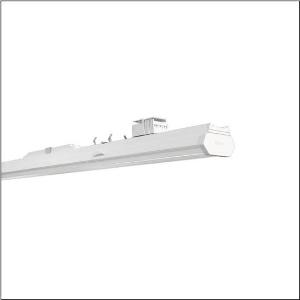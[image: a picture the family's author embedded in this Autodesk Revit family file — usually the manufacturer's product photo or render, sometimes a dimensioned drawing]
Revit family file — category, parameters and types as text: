
# Revit family: licross_11_protected_ho_51td12mn4f5m
name_source: partatom
category: Lighting Fixtures
units: mm (PartAtom-declared; Revit-internal decimal feet)

## family parameters
Cut with Voids When Loaded = No
Host = Face
Light Source = No
Part Type = Normal
Room Calculation Point = No
Round Connector Dimension = Use Diameter
Shared = No

## types (1)
- --- (1 x LED, 15820 lm, 87.4 W, 4000K)
    Apparent Load = 87 VA
    CIE Flux Codes = 70 91 97 98 100
    Color Rendering = 80
    Color Temperature = 4000K
    Default Elevation = 1800 mm
    Description = Licross 11 Protected HO, luminaire insert, of sheet steel, galvanised, coil coated, white, length: 1.500mm, width: 90mm, height: 101mm, LED rated luminous flux: 15.820lm, light colour: 840, SDCM (Standard Deviation of Colour Matching)MacAdam ≤ 2 SDCM (initial), control gear: ON/OFF Multilumen, with plug, 3-pole, with phase selection, mains connection: 220..240V, AC, 50/60Hz, rated input power: 87W, internal wiring halogen-free, primary light control with lens, of plastic, primary optical cover: cover, of PMMA, light emission: direct distribution, primary light characteristic: symmetric, protection rating (complete): IP54, insulation class (complete): insulation class I (protective earthing), certification: CE, ENEC, VDE, UKCA, protection symbol: D if used in an environment with non-conductive dust loads with corresponding accessories, impact resistance: IK06, permissible ambient temperature for indoor applications: -35..+35°C, corresponds to IFS (International Featured Standards) requirements for safety and quality in the food industry, reducing of maximum allowable ambient temperature of 5°C with ceiling mounting, LABS conformity tested according to VDMA 24364:2018-05, The light source and the operating device comply with the requirements of the Ecodesign Regulation (EU) 2019/2020 and are replaceable in accordance with this regulation, packaging unit: 1 piece
    Height = 92 mm
    Lamp = 1 x LED
    Lamp Light Flux = 15820 lm
    Lamp Power = 87.4 W
    Lamp count = 1
    Length = 1500 mm
    Luminous efficacy = 181 lm/W
    Manufacturer = Siteco
    ModVariant = No
    Model = 51TD12MN4F5M
    Mounting Place = Ceiling
    Mounting Type = Pendant
    Number of Poles = 1
    OnlyDefault = Yes
    Power Factor = 1
    Product Name = Licross 11 Protected HO
    Product group = luminaire insert | ceiling pendant
    ProductGroupID = 901
    Protection Class = Protection class I
    Protection Degree = IP 54
    RLX_Detail_Level = 1
    RLX_Emergency_Light_Flux = 0 lm
    RLX_Emergency_Type = 0
    RLX_Emergency_Type_DB = No
    RlxData = <blob elided: 22365 chars, md5=dd7a1bf5>
    Socket = socket
    Standby Power = 0 W
    System Light Flux = 15820 lm
    System Power = 87 W
    Type Comments = factory setting: luminous flux: 100 % | (A | C | E) | 203 mA
    Type Image = l_1256145.jpg
    URL = http://relux.com
    VarID = @adj_092061
    Voltage = 0 V
    Weight = 0.00 kg
    Width = 88 mm

## geometry (parser evidence)
native form markers: Blend x4, Sweep x10
no freeform markers — native parametric forms only
